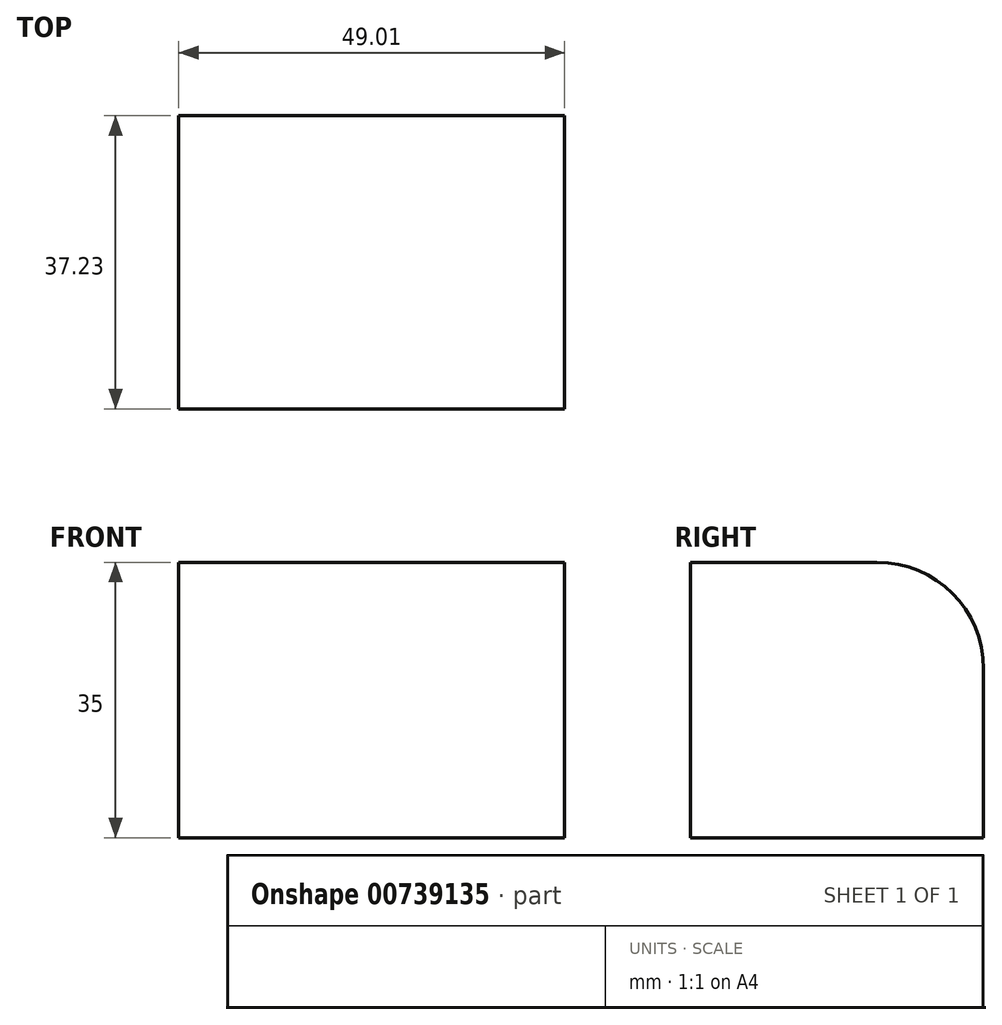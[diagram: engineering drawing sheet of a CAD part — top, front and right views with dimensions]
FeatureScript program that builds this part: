
annotation { "Feature Type Name" : "Feature", "Feature Type Description" : "" }
export const myFeature = defineFeature(function(context is Context, id is Id, definition is map)
    precondition{}
    {
        {
            var Q0;
            Q0=qCreatedBy(makeId("Top.planeOp"),FACE);
            var sketch = newSketch(context, id + "F0", { "sketchPlane" : qUnion([Q0])});
            skLineSegment(sketch, "E0.bottom", {"start": v(0, 0) * mm, "end": v(-49, 0) * mm});
            skLineSegment(sketch, "E0.top", {"start": v(0, 37.23) * mm, "end": v(-49, 37.23) * mm});
            skLineSegment(sketch, "E0.left", {"start": v(0, 0) * mm, "end": v(0, 37.23) * mm});
            skLineSegment(sketch, "E0.right", {"start": v(-49, 0) * mm, "end": v(-49, 37.23) * mm});
            skSolve(sketch);
        }
        {
            var Q0;
            Q0 = qSketchRegion(id + "F0", true);
            extrude(context, id + "F1", {"entities" : qUnion([Q0]), "depth" : 35 * mm, "offsetDistance" : 25 * mm});
        }
        {
            var Q0;
            Q0=makeQuery(id+"F1.opExtrude","CAP_EDGE",EDGE,{"disambiguationData":[OSD([sQuery(id+"F0.wireOp",EDGE,"E0.top")])],"isStart":false});
            fillet(context, id + "F2", {"entities" : qUnion([Q0]), "radius" : 13.52 * mm, "tangentPropagation" : true, "allowEdgeOverflow" : false});
        }
    });
